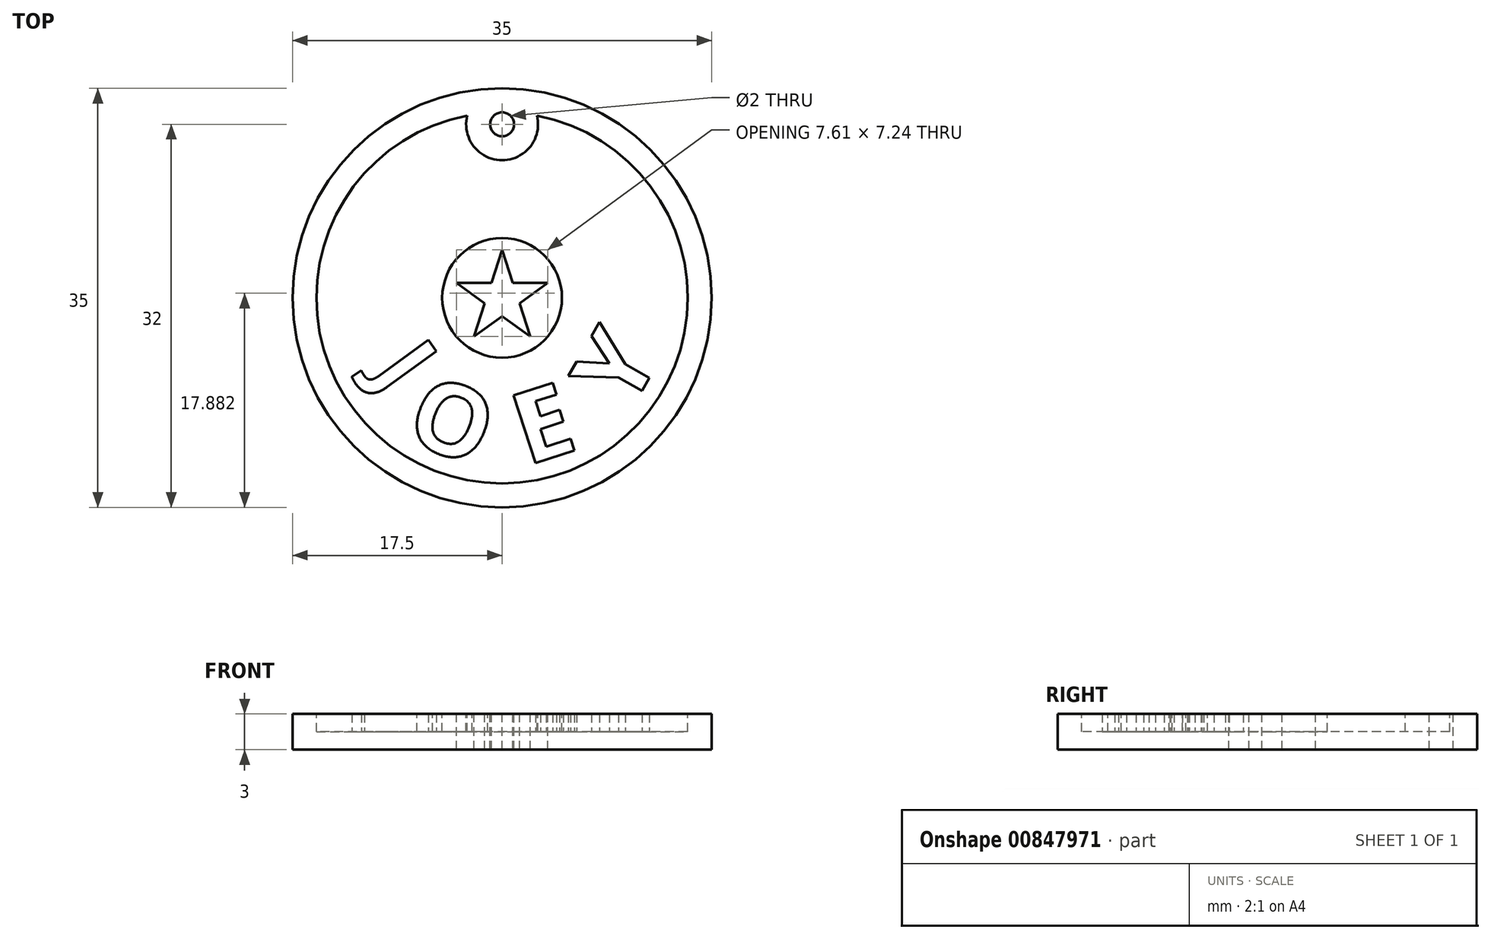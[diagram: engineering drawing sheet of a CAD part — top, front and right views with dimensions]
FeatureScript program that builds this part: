
annotation { "Feature Type Name" : "Feature", "Feature Type Description" : "" }
export const myFeature = defineFeature(function(context is Context, id is Id, definition is map)
    precondition{}
    {
        {
            var Q0;
            Q0=qCreatedBy(makeId("Top.planeOp"),FACE);
            var sketch = newSketch(context, id + "F0", { "sketchPlane" : qUnion([Q0])});
            skCircle(sketch, "E0", {"center": v(0, 0) * mm, "radius": 17.5 * mm});
            skSolve(sketch);
        }
        {
            var Q0;
            Q0 = qSketchRegion(id + "F0", true);
            extrude(context, id + "F1", {"entities" : qUnion([Q0]), "depth" : 3 * mm, "offsetDistance" : 25 * mm});
        }
        {
            var Q0;
            Q0=makeQuery(id+"F1.opExtrude","CAP_FACE",FACE,{"disambiguationData":[OSD([sQuery(id+"F0.wireOp",EDGE,"E0")])],"isStart":false});
            var sketch = newSketch(context, id + "F2", { "sketchPlane" : qUnion([Q0])});
            skCircle(sketch, "E1", {"center": v(0, 0) * mm, "radius": 5 * mm});
            skPoint(sketch, "E2", {"position": v(0, 14.5) * mm});
            skArc(sketch, "E3", {"start": v(-2.91, 15.22) * mm, "mid": v(0, -15.5) * mm, "end": v(2.91, 15.22) * mm});
            skArc(sketch, "E4", {"start": v(-2.91, 15.22) * mm, "mid": v(0, 11.5) * mm, "end": v(2.91, 15.22) * mm});
            skSolve(sketch);
        }
        {
            var Q0;
            Q0 = qSketchRegion(id + "F2", true);
            extrude(context, id + "F3", {"entities" : qUnion([Q0]), "operationType" : NewBodyOperationType.REMOVE, "oppositeDirection" : true, "depth" : 1.5 * mm, "offsetDistance" : 25 * mm});
        }
        {
            var Q0;
            {var subQ0=sQuery(id+"F0.wireOp",EDGE,"E0");Q0=makeQuery(id+"F3.boolean.opBoolean","SPLIT",FACE,{"disambiguationData":[TD([makeQuery(id+"F1.opExtrude","SWEPT_FACE",FACE,{"disambiguationData":[OSD([subQ0])]})])],"derivedFrom":makeQuery(id+"F1.opExtrude","CAP_FACE",FACE,{"disambiguationData":[OSD([subQ0])],"isStart":false})});}
            var sketch = newSketch(context, id + "F4", { "sketchPlane" : qUnion([Q0])});
            skPoint(sketch, "E5", {"position": v(0, 14.5) * mm});
            skCircle(sketch, "E6", {"center": v(0, 14.5) * mm, "radius": 1 * mm});
            skSolve(sketch);
        }
        {
            var Q0;
            Q0 = qSketchRegion(id + "F4", true);
            extrude(context, id + "F5", {"entities" : qUnion([Q0]), "operationType" : NewBodyOperationType.REMOVE, "endBound" : BoundingType.THROUGH_ALL, "oppositeDirection" : true, "depth" : 25 * mm, "offsetDistance" : 25 * mm});
        }
        {
            var Q0;
            Q0=makeQuery(id+"F3.boolean.opBoolean","SPLIT",FACE,{"disambiguationData":[TD([makeQuery(id+"F3.opExtrude","SWEPT_FACE",FACE,{"disambiguationData":[OSD([sQuery(id+"F2.wireOp",EDGE,"E1")])]})])],"derivedFrom":makeQuery(id+"F1.opExtrude","CAP_FACE",FACE,{"disambiguationData":[OSD([sQuery(id+"F0.wireOp",EDGE,"E0")])],"isStart":false})});
            var sketch = newSketch(context, id + "F6", { "sketchPlane" : qUnion([Q0])});
            skPoint(sketch, "E7", {"position": v(0, 4) * mm});
            skPoint(sketch, "E8.center", {"position": v(0, 0) * mm});
            skPoint(sketch, "E9.1.0", {"position": v(-3.8, 1.24) * mm});
            skPoint(sketch, "E9.2.0", {"position": v(-2.35, -3.24) * mm});
            skPoint(sketch, "E10.0.3.0", {"position": v(2.35, -3.24) * mm});
            skPoint(sketch, "E10.0.4.0", {"position": v(3.8, 1.24) * mm});
            skLineSegment(sketch, "E11", {"start": v(0, 4) * mm, "end": v(-0.9, 1.24) * mm});
            skLineSegment(sketch, "E12", {"start": v(-2.35, -3.24) * mm, "end": v(0, -1.53) * mm});
            skLineSegment(sketch, "E13", {"start": v(3.8, 1.24) * mm, "end": v(0.9, 1.24) * mm});
            skLineSegment(sketch, "E14", {"start": v(-3.8, 1.24) * mm, "end": v(-1.45, -0.47) * mm});
            skLineSegment(sketch, "E15", {"start": v(2.35, -3.24) * mm, "end": v(1.45, -0.47) * mm});
            skLineSegment(sketch, "E16.trimOffspring", {"start": v(-0.9, 1.24) * mm, "end": v(-3.8, 1.24) * mm});
            skLineSegment(sketch, "E17.trimOffspring", {"start": v(-1.45, -0.47) * mm, "end": v(-2.35, -3.24) * mm});
            skLineSegment(sketch, "E18.trimOffspring", {"start": v(0, -1.53) * mm, "end": v(2.35, -3.24) * mm});
            skLineSegment(sketch, "E19.trimOffspring", {"start": v(1.45, -0.47) * mm, "end": v(3.8, 1.24) * mm});
            skLineSegment(sketch, "E20.trimOffspring", {"start": v(0.9, 1.24) * mm, "end": v(0, 4) * mm});
            skSolve(sketch);
        }
        {
            var Q0;
            Q0 = qSketchRegion(id + "F6", true);
            extrude(context, id + "F7", {"entities" : qUnion([Q0]), "operationType" : NewBodyOperationType.REMOVE, "endBound" : BoundingType.THROUGH_ALL, "oppositeDirection" : true, "depth" : 25 * mm, "offsetDistance" : 25 * mm});
        }
        {
            var Q0;
            Q0=makeQuery(id+"F3.boolean.opBoolean","COPY",FACE,{"derivedFrom":makeQuery(id+"F3.opExtrude","CAP_FACE",FACE,{"disambiguationData":[OSD([sQuery(id+"F2.wireOp",EDGE,"E1"),sQuery(id+"F2.wireOp",EDGE,"E3"),sQuery(id+"F2.wireOp",EDGE,"E4")])],"isStart":false})});
            var sketch = newSketch(context, id + "F8", { "sketchPlane" : qUnion([Q0])});
            skLineSegment(sketch, "E21", {"start": v(0, 0) * mm, "end": v(-7.69, -5.59) * mm});
            skLineSegment(sketch, "E22", {"start": v(0, 0) * mm, "end": v(-3.44, -8.52) * mm});
            skLineSegment(sketch, "E23", {"start": v(0, 0) * mm, "end": v(3.3, -10.15) * mm});
            skLineSegment(sketch, "E24", {"start": v(0, 0) * mm, "end": v(8.55, -4.93) * mm});
            skText(sketch, "E25", { "text": "O", "fontName": "OpenSans-Bold.ttf"});
            skText(sketch, "E26", { "text": "E", "fontName": "OpenSans-Bold.ttf"});
            skText(sketch, "E27", { "text": "Y", "fontName": "OpenSans-Bold.ttf"});
            skText(sketch, "E28", { "text": "J", "fontName": "OpenSans-Bold.ttf"});
            const initialGuessF8  = {"E25": [-0.00835, -0.01173, 0.92718, -0.3746, 0.006], "E26": [0.00208, -0.01404, 0.95106, 0.30902, 0.006], "E27": [0.01069, -0.00949, 0.5, 0.86603, 0.006], "E28": [-0.01097, -0.00617, 0.58779, -0.80902, 0.0055]};
            skSetInitialGuess(sketch, initialGuessF8);
            skSolve(sketch);
        }
        {
            var Q0;
            Q0 = qSketchRegion(id + "F8", true);
            extrude(context, id + "F9", {"entities" : qUnion([Q0]), "operationType" : NewBodyOperationType.ADD, "depth" : 1.5 * mm, "offsetDistance" : 25 * mm});
        }
    });
